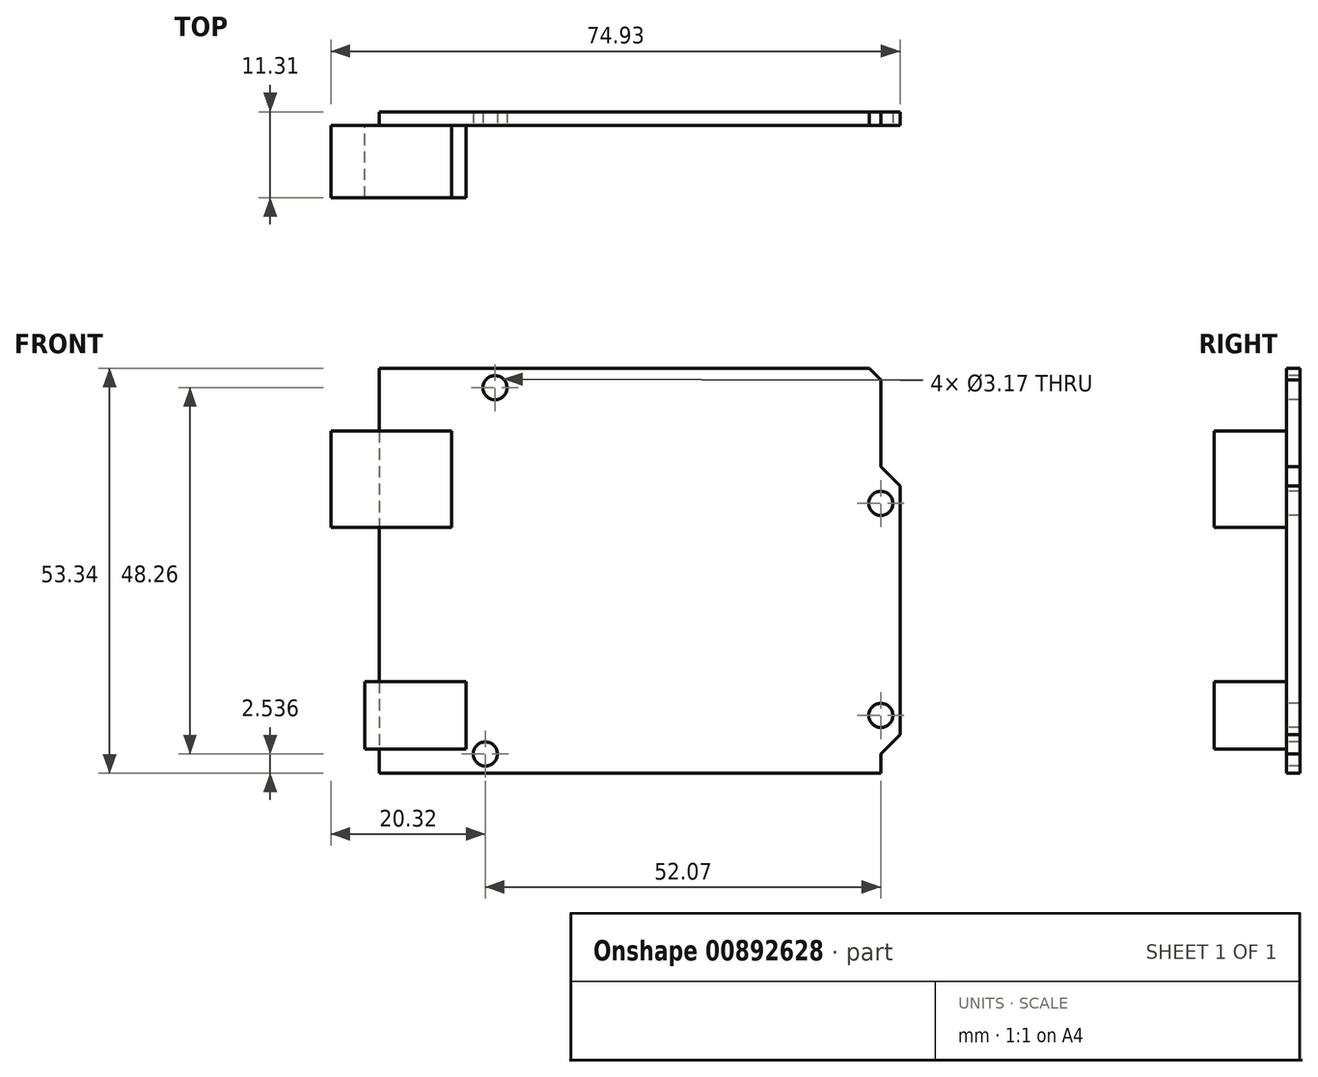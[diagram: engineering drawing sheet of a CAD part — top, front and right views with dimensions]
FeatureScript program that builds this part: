
annotation { "Feature Type Name" : "Feature", "Feature Type Description" : "" }
export const myFeature = defineFeature(function(context is Context, id is Id, definition is map)
    precondition{}
    {
        {
            var Q0;
            Q0=qCreatedBy(makeId("Front.planeOp"),FACE);
            var sketch = newSketch(context, id + "F0", { "sketchPlane" : qUnion([Q0])});
            skLineSegment(sketch, "E0", {"start": v(-48.13, 60.12) * mm, "end": v(16.39, 60.12) * mm});
            skLineSegment(sketch, "E1", {"start": v(-48.13, 60.12) * mm, "end": v(-48.13, 6.78) * mm});
            skLineSegment(sketch, "E2", {"start": v(-48.13, 6.78) * mm, "end": v(17.91, 6.78) * mm});
            skLineSegment(sketch, "E3", {"start": v(17.91, 6.78) * mm, "end": v(17.91, 9.32) * mm});
            skLineSegment(sketch, "E4", {"start": v(17.91, 58.6) * mm, "end": v(17.91, 47.16) * mm});
            skLineSegment(sketch, "E5", {"start": v(17.91, 47.16) * mm, "end": v(20.45, 44.62) * mm});
            skLineSegment(sketch, "E6", {"start": v(20.45, 44.62) * mm, "end": v(20.45, 11.86) * mm});
            skLineSegment(sketch, "E7", {"start": v(17.91, 9.32) * mm, "end": v(20.45, 11.86) * mm});
            skLineSegment(sketch, "E8", {"start": v(16.39, 60.12) * mm, "end": v(17.91, 58.6) * mm});
            skCircle(sketch, "E9", {"center": v(-34.16, 9.32) * mm, "radius": 1.59 * mm});
            skPoint(sketch, "E10", {"position": v(-48.13, 38.33) * mm});
            skCircle(sketch, "E11", {"center": v(17.91, 42.34) * mm, "radius": 1.59 * mm});
            skCircle(sketch, "E12", {"center": v(17.91, 14.4) * mm, "radius": 1.59 * mm});
            skCircle(sketch, "E13", {"center": v(-32.89, 57.58) * mm, "radius": 1.59 * mm});
            skPoint(sketch, "E14.top.end.orphan", {"position": v(-38.6, 39.16) * mm});
            skPoint(sketch, "E15.top.end.orphan", {"position": v(-36.7, 9.95) * mm});
            skSolve(sketch);
        }
        {
            var Q0;
            Q0=makeQuery(id+"F0.imprint","IMPRINT",FACE,{"disambiguationData":[TD([[makeQuery(id+"F0.imprint","IMPRINT",EDGE,{"derivedFrom":sQuery(id+"F0.wireOp",EDGE,"E0")}),-1.0]])]});
            var sketch = newSketch(context, id + "F1", { "sketchPlane" : qUnion([Q0])});
            skLineSegment(sketch, "E16.bottom", {"start": v(-54.48, 51.86) * mm, "end": v(-38.6, 51.86) * mm});
            skLineSegment(sketch, "E16.top", {"start": v(-54.48, 39.16) * mm, "end": v(-38.6, 39.16) * mm});
            skLineSegment(sketch, "E16.left", {"start": v(-54.48, 51.86) * mm, "end": v(-54.48, 39.16) * mm});
            skLineSegment(sketch, "E16.right", {"start": v(-38.6, 51.86) * mm, "end": v(-38.6, 39.16) * mm});
            skLineSegment(sketch, "E17.bottom", {"start": v(-50.03, 18.84) * mm, "end": v(-36.7, 18.84) * mm});
            skLineSegment(sketch, "E17.top", {"start": v(-50.03, 9.95) * mm, "end": v(-36.7, 9.95) * mm});
            skLineSegment(sketch, "E17.left", {"start": v(-50.03, 18.84) * mm, "end": v(-50.03, 9.95) * mm});
            skLineSegment(sketch, "E17.right", {"start": v(-36.7, 18.84) * mm, "end": v(-36.7, 9.95) * mm});
            skSolve(sketch);
        }
        {
            var Q0;
            Q0=makeQuery(id+"F0.imprint","IMPRINT",FACE,{"disambiguationData":[TD([[makeQuery(id+"F0.imprint","IMPRINT",EDGE,{"derivedFrom":sQuery(id+"F0.wireOp",EDGE,"E0")}),-1.0]])]});
            extrude(context, id + "F2", {"entities" : qUnion([Q0]), "oppositeDirection" : true, "depth" : 1.78 * mm, "offsetDistance" : 25.4 * mm});
        }
        {
            var Q0;
            Q0=makeQuery(id+"F1.imprint","IMPRINT",FACE,{"disambiguationData":[TD([[makeQuery(id+"F1.imprint","IMPRINT",EDGE,{"derivedFrom":sQuery(id+"F1.wireOp",EDGE,"E16.bottom")}),-1.0]])]});
            var Q1;
            Q1=makeQuery(id+"F1.imprint","IMPRINT",FACE,{"disambiguationData":[TD([[makeQuery(id+"F1.imprint","IMPRINT",EDGE,{"derivedFrom":sQuery(id+"F1.wireOp",EDGE,"E17.bottom")}),-1.0]])]});
            extrude(context, id + "F3", {"entities" : qUnion([Q0, Q1]), "depth" : 9.52 * mm, "offsetDistance" : 25.4 * mm});
        }
    });
